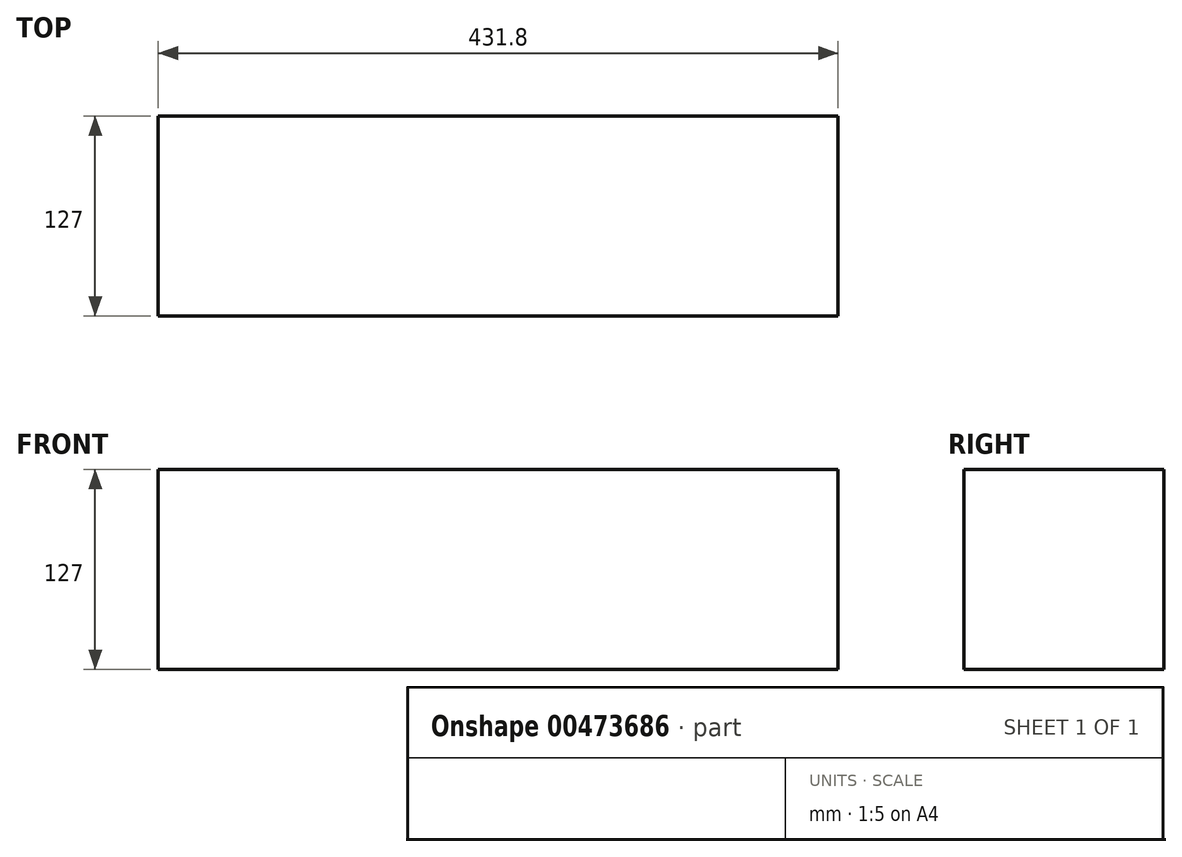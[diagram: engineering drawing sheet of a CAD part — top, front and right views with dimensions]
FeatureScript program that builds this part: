
annotation { "Feature Type Name" : "Feature", "Feature Type Description" : "" }
export const myFeature = defineFeature(function(context is Context, id is Id, definition is map)
    precondition{}
    {
        {
            var Q0;
            Q0=qCreatedBy(makeId("Front.planeOp"),FACE);
            var sketch = newSketch(context, id + "F0", { "sketchPlane" : qUnion([Q0])});
            skLineSegment(sketch, "E0.bottom", {"start": v(215.9, -63.5) * mm, "end": v(-215.9, -63.5) * mm});
            skLineSegment(sketch, "E0.top", {"start": v(215.9, 63.5) * mm, "end": v(-215.9, 63.5) * mm});
            skLineSegment(sketch, "E0.left", {"start": v(215.9, -63.5) * mm, "end": v(215.9, 63.5) * mm});
            skLineSegment(sketch, "E0.right", {"start": v(-215.9, -63.5) * mm, "end": v(-215.9, 63.5) * mm});
            skPoint(sketch, "E0.middle", {"position": v(0, 0) * mm});
            skSolve(sketch);
        }
        {
            var Q0;
            Q0=qSketchRegion(id+"F0",true);
            extrude(context, id + "F1", {"entities" : qUnion([Q0]), "depth" : 127 * mm});
        }
    });
